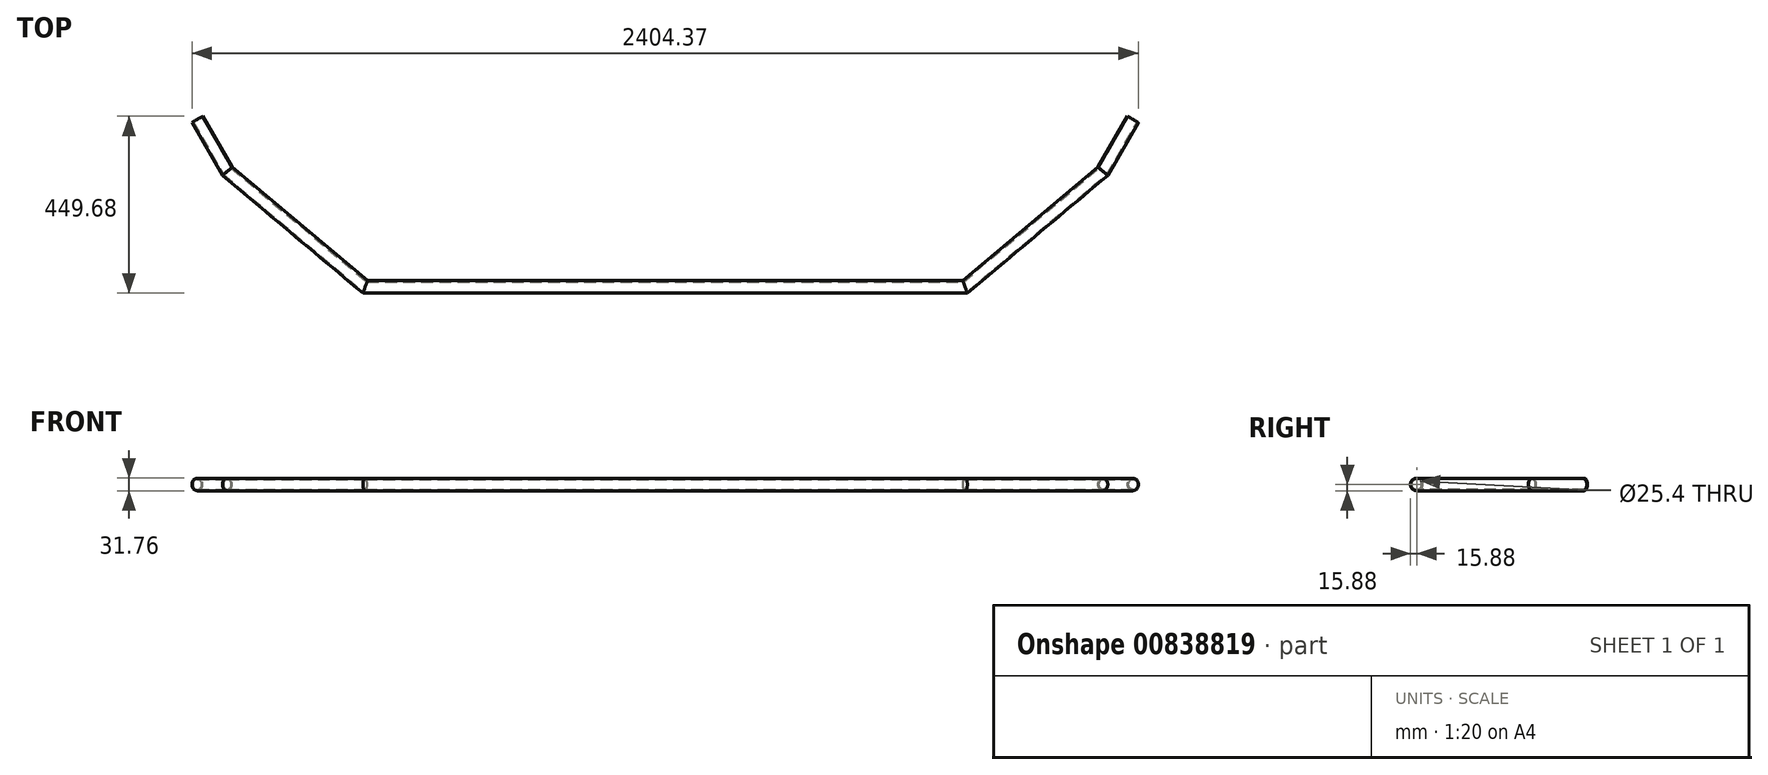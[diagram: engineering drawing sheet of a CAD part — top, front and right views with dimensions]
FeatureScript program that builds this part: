
annotation { "Feature Type Name" : "Feature", "Feature Type Description" : "" }
export const myFeature = defineFeature(function(context is Context, id is Id, definition is map)
    precondition{}
    {
        {
            var Q0;
            Q0=qCreatedBy(makeId("Top.planeOp"),FACE);
            var sketch = newSketch(context, id + "F0", { "sketchPlane" : qUnion([Q0])});
            skLineSegment(sketch, "E0", {"start": v(-396.97, 293.88) * mm, "end": v(-46.74, 0) * mm});
            skLineSegment(sketch, "E1", {"start": v(-46.74, 0) * mm, "end": v(1477.26, 0) * mm});
            skLineSegment(sketch, "E2", {"start": v(1477.26, 0) * mm, "end": v(1827.5, 293.88) * mm});
            skLineSegment(sketch, "E3", {"start": v(-396.97, 293.88) * mm, "end": v(-473.17, 425.86) * mm});
            skLineSegment(sketch, "E4", {"start": v(1827.5, 293.88) * mm, "end": v(1903.7, 425.86) * mm});
            skSolve(sketch);
        }
        {
            var Q0;
            Q0=qCreatedBy(makeId("Right.planeOp"),FACE);
            var sketch = newSketch(context, id + "F1", { "sketchPlane" : qUnion([Q0])});
            skCircle(sketch, "E5", {"center": v(0, 0) * mm, "radius": 15.88 * mm});
            skCircle(sketch, "E6", {"center": v(0, 0) * mm, "radius": 12.7 * mm});
            skSolve(sketch);
        }
        {
            var Q0;
            Q0 = qSketchRegion(id + "F1", true);
            var Q1;
            Q1=sQuery(id+"F0.wireOp",EDGE,"E3");
            var Q2;
            Q2=sQuery(id+"F0.wireOp",EDGE,"E1");
            var Q3;
            Q3=sQuery(id+"F0.wireOp",EDGE,"E0");
            var Q4;
            Q4=sQuery(id+"F0.wireOp",EDGE,"E2");
            var Q5;
            Q5=sQuery(id+"F0.wireOp",EDGE,"E4");
            sweep(context, id + "F2", {"profiles" : qUnion([Q0]), "path" : qUnion([Q1, Q2, Q3, Q4, Q5])});
        }
    });
